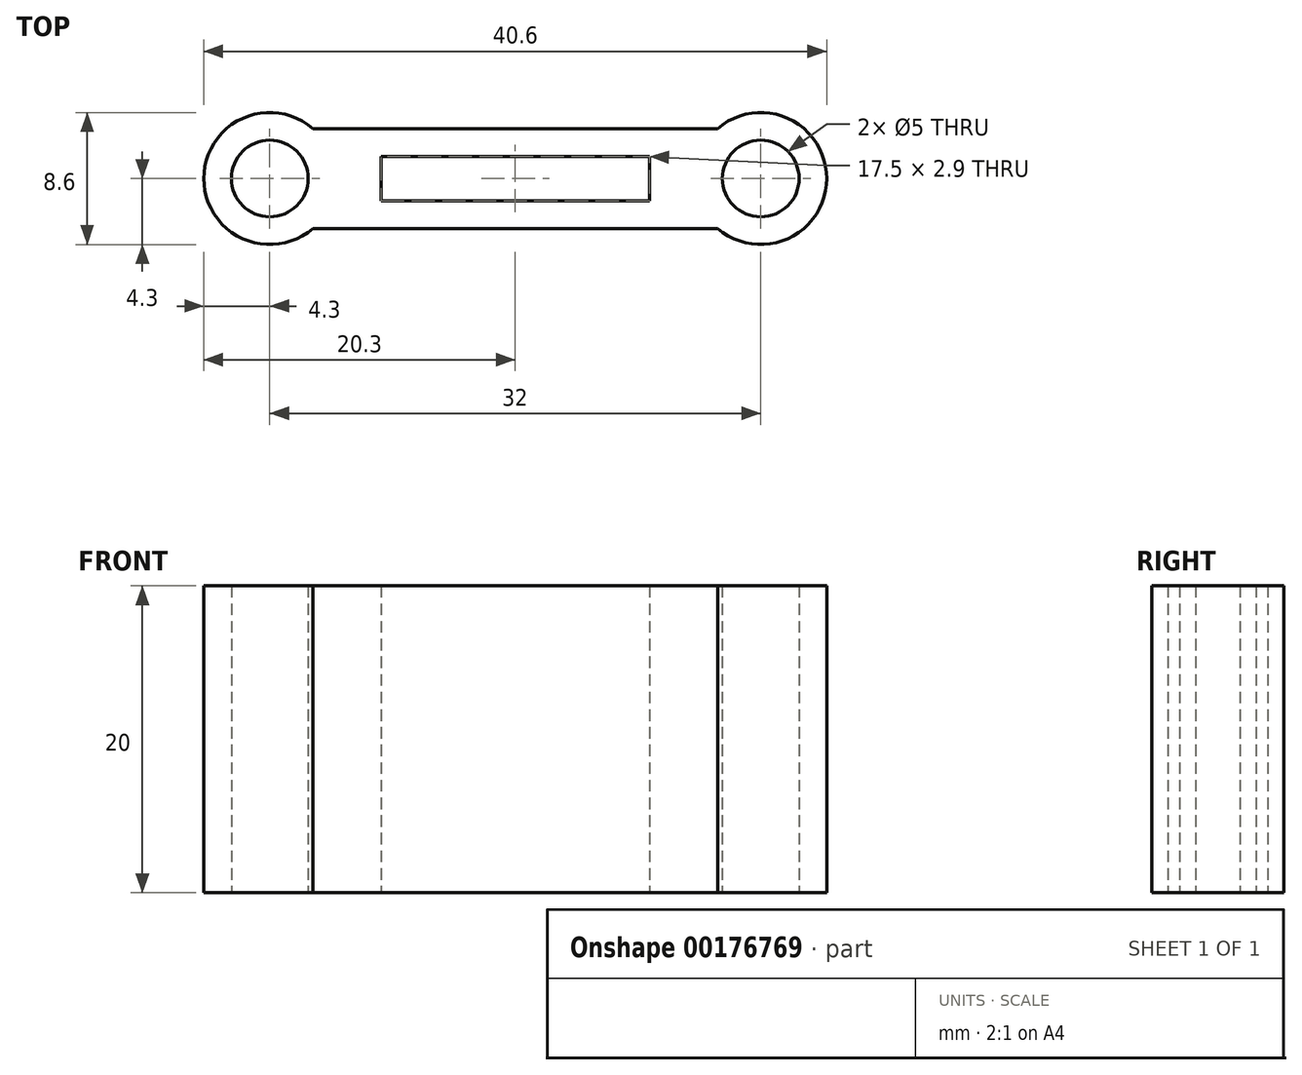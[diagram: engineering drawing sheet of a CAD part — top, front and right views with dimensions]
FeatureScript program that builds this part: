
annotation { "Feature Type Name" : "Feature", "Feature Type Description" : "" }
export const myFeature = defineFeature(function(context is Context, id is Id, definition is map)
    precondition{}
    {
        {
            assignVariable(context, id + "F0", {"name" : "pieceHeight", "anyValue" : 20});
        }
        {
            var Q0;
            Q0=qCreatedBy(makeId("Top.planeOp"),FACE);
            var sketch = newSketch(context, id + "F1", { "sketchPlane" : qUnion([Q0])});
            skCircle(sketch, "E0", {"center": v(-16, 0) * mm, "radius": 2.5 * mm});
            skCircle(sketch, "E1", {"center": v(16, 0) * mm, "radius": 2.5 * mm});
            skCircle(sketch, "E2.0", {"center": v(-16, 0) * mm, "radius": 4.3 * mm});
            skCircle(sketch, "E3.0", {"center": v(16, 0) * mm, "radius": 4.3 * mm});
            skLineSegment(sketch, "E4", {"start": v(-16, 0) * mm, "end": v(16, 0) * mm, "construction": true});
            skLineSegment(sketch, "E5.bottom", {"start": v(-8.75, 1.45) * mm, "end": v(8.75, 1.45) * mm});
            skLineSegment(sketch, "E5.top", {"start": v(-8.75, -1.45) * mm, "end": v(8.75, -1.45) * mm});
            skLineSegment(sketch, "E5.left", {"start": v(-8.75, 1.45) * mm, "end": v(-8.75, -1.45) * mm});
            skLineSegment(sketch, "E5.right", {"start": v(8.75, 1.45) * mm, "end": v(8.75, -1.45) * mm});
            skPoint(sketch, "E5.middle", {"position": v(0, 0) * mm});
            skLineSegment(sketch, "E6", {"start": v(-13.18, 3.25) * mm, "end": v(13.18, 3.25) * mm});
            skLineSegment(sketch, "E7", {"start": v(-13.18, -3.25) * mm, "end": v(13.18, -3.25) * mm});
            skSolve(sketch);
        }
        {
            var Q0;
            Q0 = qSketchRegion(id + "F1", true);
            extrude(context, id + "F2", {"entities" : qUnion([Q0]), "depth" : (getVariable(context, 'pieceHeight')) * mm});
        }
    });
